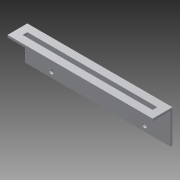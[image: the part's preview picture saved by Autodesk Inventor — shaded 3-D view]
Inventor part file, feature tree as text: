
AUTODESK INVENTOR PART (.ipt)
format: ipt  version: 2015 (Build 190159000, 159)  size: 135,168 bytes
history: native  units: mm
features: sketch x4, extrude x3, other x1, hole x1
ambient origin geometry x8: Origin, YZ Plane, XZ Plane, XY Plane, X Axis, Y Axis, Z Axis, Center Point
bodies: Body1 (feature_tree)
feature tree (9):
  other  "ソリッド1"
  extrude  "押し出し1"  Depth=11.5mm
  extrude  "押し出し2"  Depth=95.0mm
  extrude  "押し出し3"  Depth=1.5mm TaperAngle=0.0deg
  hole  "穴1"  [1 undecoded]
  sketch  "スケッチ1"
  sketch  "スケッチ2"
  sketch  "スケッチ3"
  sketch  "スケッチ4"
note: 1 required parameter value undecoded (feature->parameter linkage not recoverable at this tier; creation-order binding heuristic only, values carry confidence <= 0.55)
